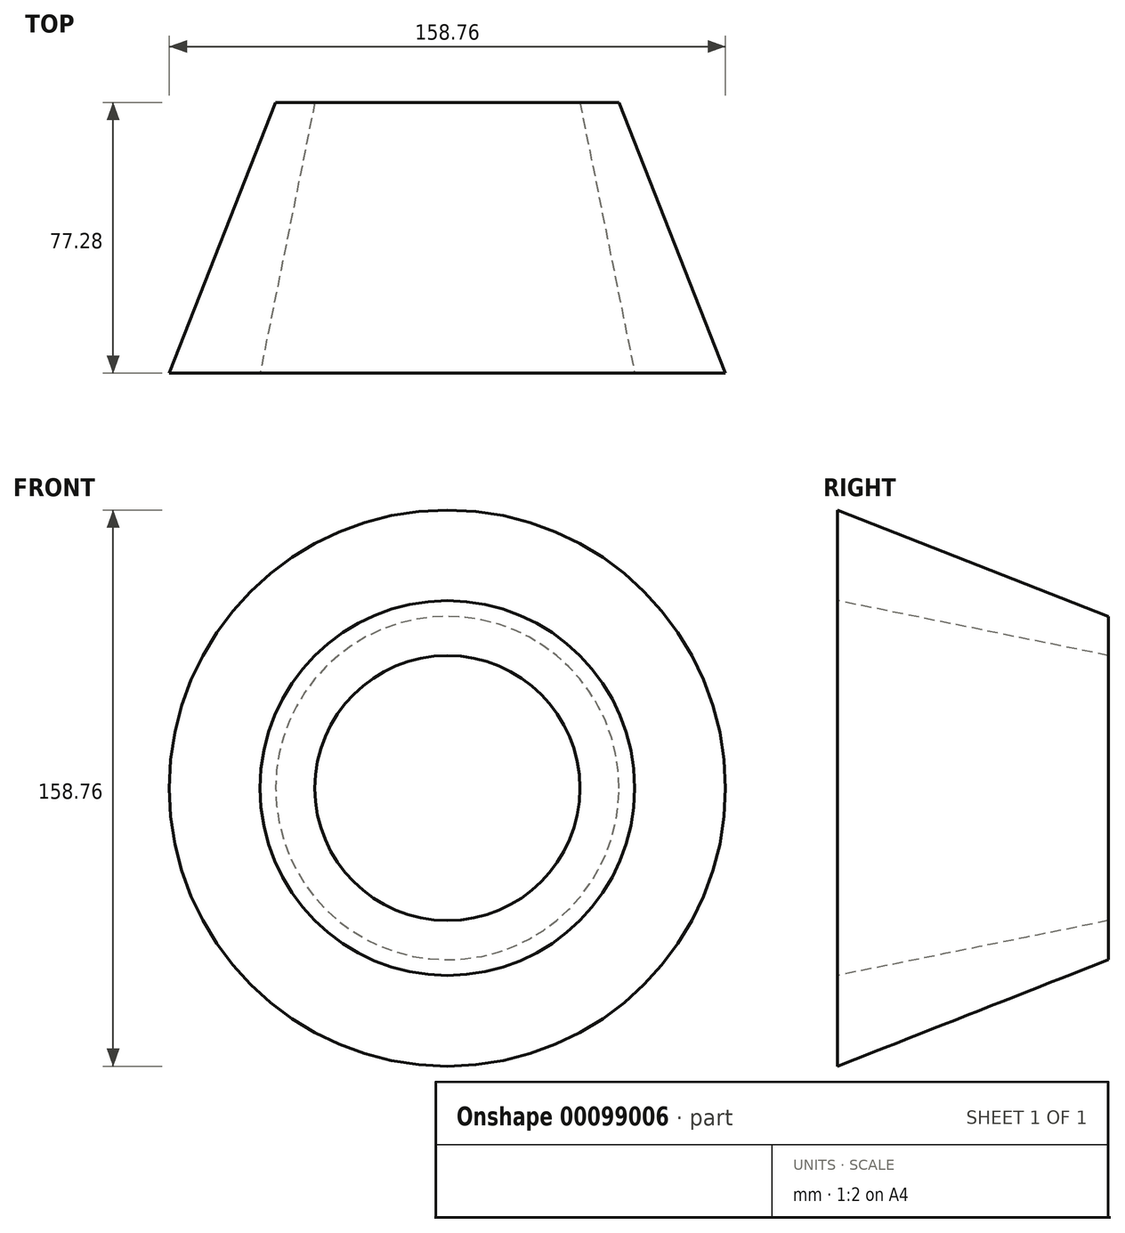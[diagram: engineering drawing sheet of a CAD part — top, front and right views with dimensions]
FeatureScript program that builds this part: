
annotation { "Feature Type Name" : "Feature", "Feature Type Description" : "" }
export const myFeature = defineFeature(function(context is Context, id is Id, definition is map)
    precondition{}
    {
        {
            var Q0;
            Q0=qCreatedBy(makeId("Right.planeOp"),FACE);
            var sketch = newSketch(context, id + "F0", { "sketchPlane" : qUnion([Q0])});
            skLineSegment(sketch, "E0", {"start": v(0, 0) * mm, "end": v(77.28, 0) * mm, "construction": true});
            skLineSegment(sketch, "E1", {"start": v(0, 53.48) * mm, "end": v(77.28, 37.83) * mm});
            skLineSegment(sketch, "E2", {"start": v(77.28, 37.83) * mm, "end": v(77.28, 49) * mm});
            skLineSegment(sketch, "E3", {"start": v(77.28, 49) * mm, "end": v(0, 79.38) * mm});
            skLineSegment(sketch, "E4", {"start": v(0, 79.38) * mm, "end": v(0, 53.48) * mm});
            skSolve(sketch);
        }
        {
            var Q0;
            Q0=makeQuery(id+"F0.imprint","IMPRINT",FACE,{"disambiguationData":[TD([[makeQuery(id+"F0.imprint","IMPRINT",EDGE,{"derivedFrom":sQuery(id+"F0.wireOp",EDGE,"E1")}),1.0]])]});
            var Q1;
            Q1=sQuery(id+"F0.wireOp",EDGE,"E0");
            revolve(context, id + "F1", {"entities" : qUnion([Q0]), "axis" : qUnion([Q1]), "revolveType" : RevolveType.FULL});
        }
    });
